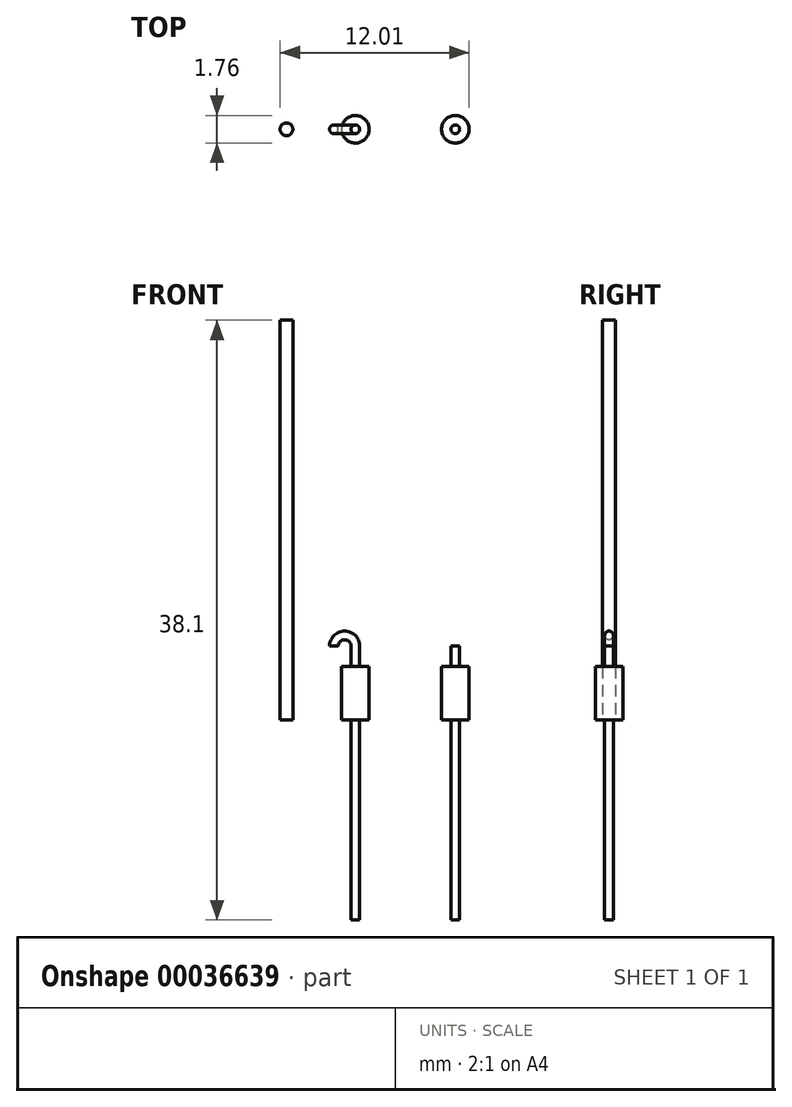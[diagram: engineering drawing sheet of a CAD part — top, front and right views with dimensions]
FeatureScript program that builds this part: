
annotation { "Feature Type Name" : "Feature", "Feature Type Description" : "" }
export const myFeature = defineFeature(function(context is Context, id is Id, definition is map)
    precondition{}
    {
        {
            var Q0;
            Q0=qCreatedBy(makeId("Top.planeOp"),FACE);
            var sketch = newSketch(context, id + "F0", { "sketchPlane" : qUnion([Q0])});
            skCircle(sketch, "E0", {"center": v(0, 0) * mm, "radius": 0.87 * mm});
            skCircle(sketch, "E1", {"center": v(0, 0) * mm, "radius": 0.28 * mm});
            skCircle(sketch, "E2", {"center": v(-4.38, 0) * mm, "radius": 0.4 * mm});
            skSolve(sketch);
        }
        {
            var Q0;
            Q0=makeQuery(id+"F0.imprint","IMPRINT",FACE,{"disambiguationData":[TD([[makeQuery(id+"F0.imprint","IMPRINT",EDGE,{"derivedFrom":sQuery(id+"F0.wireOp",EDGE,"E1")}),1.0]])]});
            var Q1;
            Q1=makeQuery(id+"F0.imprint","IMPRINT",FACE,{"disambiguationData":[TD([[makeQuery(id+"F0.imprint","IMPRINT",EDGE,{"derivedFrom":sQuery(id+"F0.wireOp",EDGE,"E0")}),1.0]])]});
            extrude(context, id + "F1", {"entities" : qUnion([Q0, Q1]), "depth" : 3.4 * mm});
        }
        {
            var Q0;
            Q0=makeQuery(id+"F0.imprint","IMPRINT",FACE,{"disambiguationData":[TD([[makeQuery(id+"F0.imprint","IMPRINT",EDGE,{"derivedFrom":sQuery(id+"F0.wireOp",EDGE,"E1")}),1.0]])]});
            extrude(context, id + "F2", {"entities" : qUnion([Q0]), "operationType" : NewBodyOperationType.ADD, "oppositeDirection" : true, "depth" : 12.7 * mm});
        }
        {
            var Q0;
            Q0=makeQuery(id+"F0.imprint","IMPRINT",FACE,{"disambiguationData":[TD([[makeQuery(id+"F0.imprint","IMPRINT",EDGE,{"derivedFrom":sQuery(id+"F0.wireOp",EDGE,"E1")}),1.0]])]});
            extrude(context, id + "F3", {"entities" : qUnion([Q0]), "operationType" : NewBodyOperationType.ADD, "depth" : 4.7 * mm});
        }
        {
            var Q0;
            Q0=makeQuery(id+"F1.opExtrude","SWEPT_BODY",BODY,{"disambiguationData":[OSD([sQuery(id+"F0.wireOp",EDGE,"E0")])]});
            transform(context, id + "F4", {"entities" : qUnion([Q0]), "transformType" : TransformType.TRANSLATION_3D, "dx" : 6.35 * mm, "dy" : 0 * mm, "dz" : 0 * mm, "makeCopy" : true});
        }
        {
            var Q0;
            Q0=qCreatedBy(makeId("Front.planeOp"),FACE);
            var sketch = newSketch(context, id + "F5", { "sketchPlane" : qUnion([Q0])});
            skLineSegment(sketch, "E3", {"start": v(0, 4.7) * mm, "end": v(-0.28, 4.7) * mm});
            skCircle(sketch, "E4", {"center": v(-0.68, 4.7) * mm, "radius": 0.4 * mm});
            skSolve(sketch);
        }
        {
            var Q0;
            Q0=makeQuery(id+"F3.opExtrude","CAP_FACE",FACE,{"disambiguationData":[OSD([sQuery(id+"F0.wireOp",EDGE,"E1")])],"isStart":false});
            var Q1;
            Q1=sQuery(id+"F5.wireOp",EDGE,"E4");
            revolve(context, id + "F6", {"operationType" : NewBodyOperationType.ADD, "entities" : qUnion([Q0]), "axis" : qUnion([Q1]), "revolveType" : RevolveType.ONE_DIRECTION, "angle" : 180 * degree});
        }
        {
            var Q0;
            Q0=makeQuery(id+"F0.imprint","IMPRINT",FACE,{"disambiguationData":[TD([[makeQuery(id+"F0.imprint","IMPRINT",EDGE,{"derivedFrom":sQuery(id+"F0.wireOp",EDGE,"E2")}),1.0]])]});
            extrude(context, id + "F7", {"entities" : qUnion([Q0]), "depth" : 25.4 * mm});
        }
    });
